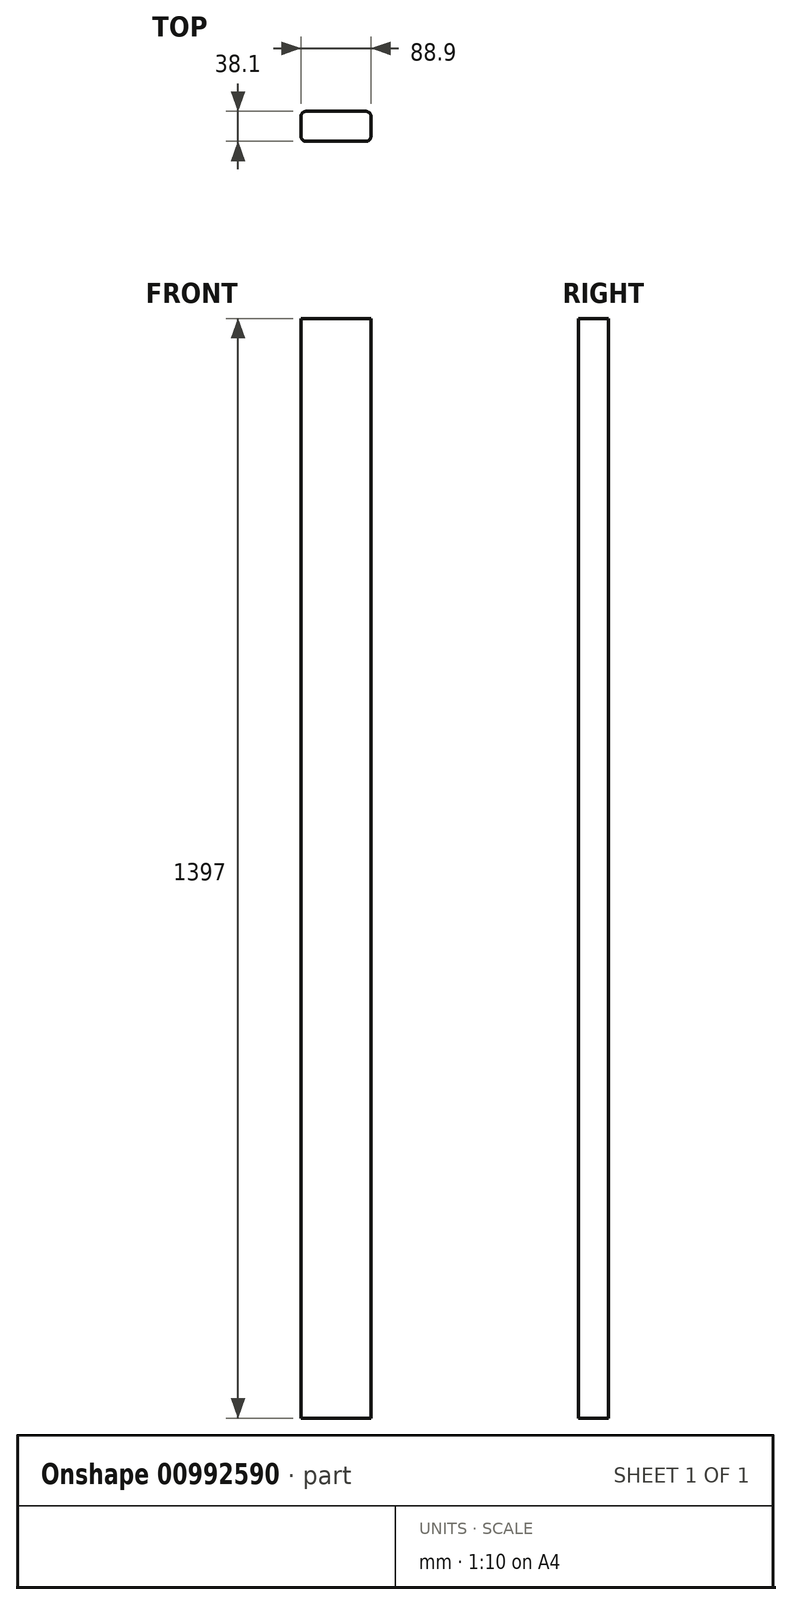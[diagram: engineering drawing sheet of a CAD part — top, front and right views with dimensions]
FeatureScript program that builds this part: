
annotation { "Feature Type Name" : "Feature", "Feature Type Description" : "" }
export const myFeature = defineFeature(function(context is Context, id is Id, definition is map)
    precondition{}
    {
        {
            var Q0;
            Q0=qCreatedBy(makeId("Top.planeOp"),FACE);
            var sketch = newSketch(context, id + "F0", { "sketchPlane" : qUnion([Q0])});
            skLineSegment(sketch, "E0.bottom", {"start": v(-44.45, 19.05) * mm, "end": v(44.45, 19.05) * mm});
            skLineSegment(sketch, "E0.top", {"start": v(-44.45, -19.05) * mm, "end": v(44.45, -19.05) * mm});
            skLineSegment(sketch, "E0.left", {"start": v(-44.45, 19.05) * mm, "end": v(-44.45, -19.05) * mm});
            skLineSegment(sketch, "E0.right", {"start": v(44.45, 19.05) * mm, "end": v(44.45, -19.05) * mm});
            skSolve(sketch);
        }
        {
            var Q0;
            Q0 = qSketchRegion(id + "F0", true);
            extrude(context, id + "F1", {"entities" : qUnion([Q0]), "depth" : 1397 * mm, "offsetDistance" : 25.4 * mm});
        }
        {
            var Q0;
            Q0=makeQuery(id+"F1.opExtrude","SWEPT_EDGE",EDGE,{"disambiguationData":[OSD([sQuery(id+"F0.wireOp",EDGE,"E0.top"),sQuery(id+"F0.wireOp",EDGE,"E0.left")])]});
            var Q1;
            Q1=makeQuery(id+"F1.opExtrude","SWEPT_EDGE",EDGE,{"disambiguationData":[OSD([sQuery(id+"F0.wireOp",EDGE,"E0.top"),sQuery(id+"F0.wireOp",EDGE,"E0.right")])]});
            var Q2;
            Q2=makeQuery(id+"F1.opExtrude","SWEPT_EDGE",EDGE,{"disambiguationData":[OSD([sQuery(id+"F0.wireOp",EDGE,"E0.bottom"),sQuery(id+"F0.wireOp",EDGE,"E0.right")])]});
            var Q3;
            Q3=makeQuery(id+"F1.opExtrude","SWEPT_EDGE",EDGE,{"disambiguationData":[OSD([sQuery(id+"F0.wireOp",EDGE,"E0.bottom"),sQuery(id+"F0.wireOp",EDGE,"E0.left")])]});
            fillet(context, id + "F2", {"entities" : qUnion([Q0, Q1, Q2, Q3]), "radius" : 6.35 * mm, "tangentPropagation" : true, "allowEdgeOverflow" : false});
        }
    });
